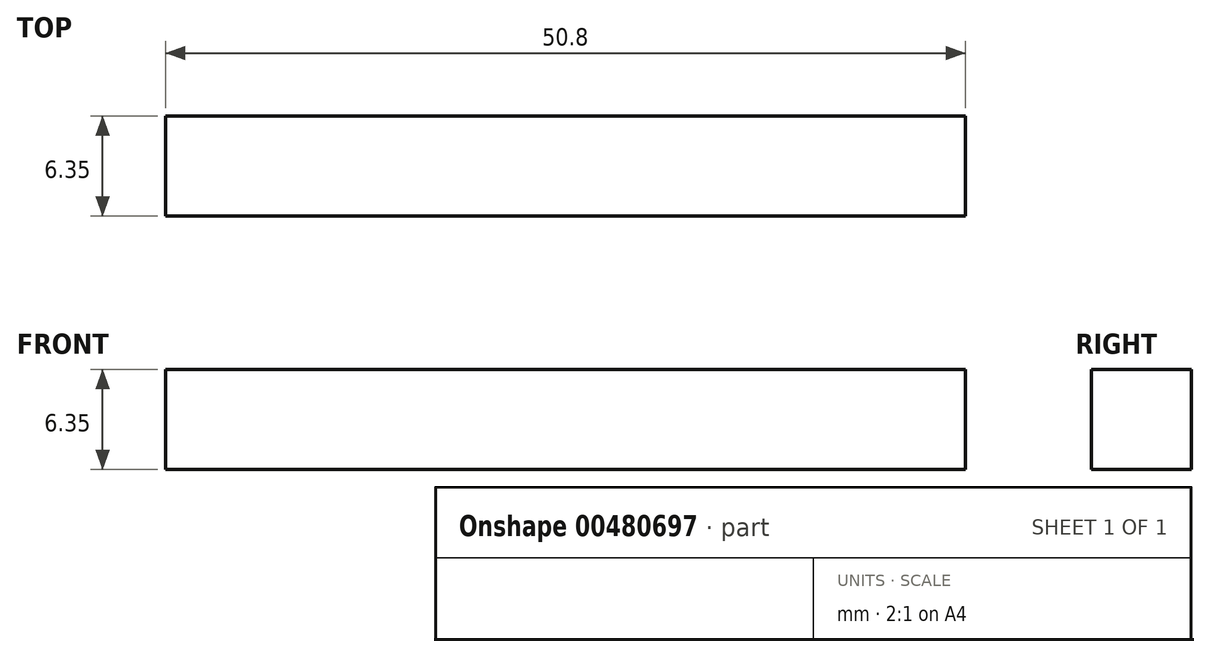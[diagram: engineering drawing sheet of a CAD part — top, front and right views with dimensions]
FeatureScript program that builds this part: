
annotation { "Feature Type Name" : "Feature", "Feature Type Description" : "" }
export const myFeature = defineFeature(function(context is Context, id is Id, definition is map)
    precondition{}
    {
        {
            var Q0;
            Q0=qCreatedBy(makeId("Front.planeOp"),FACE);
            var sketch = newSketch(context, id + "F0", { "sketchPlane" : qUnion([Q0])});
            skLineSegment(sketch, "E0.bottom", {"start": v(46.4, 2.6) * mm, "end": v(-4.4, 2.6) * mm});
            skLineSegment(sketch, "E0.top", {"start": v(46.4, 8.96) * mm, "end": v(-4.4, 8.96) * mm});
            skLineSegment(sketch, "E0.left", {"start": v(46.4, 2.6) * mm, "end": v(46.4, 8.96) * mm});
            skLineSegment(sketch, "E0.right", {"start": v(-4.4, 2.6) * mm, "end": v(-4.4, 8.96) * mm});
            skSolve(sketch);
        }
        {
            var Q0;
            Q0 = qSketchRegion(id + "F0", true);
            extrude(context, id + "F1", {"entities" : qUnion([Q0]), "depth" : 6.35 * mm, "offsetDistance" : 25.4 * mm});
        }
    });
